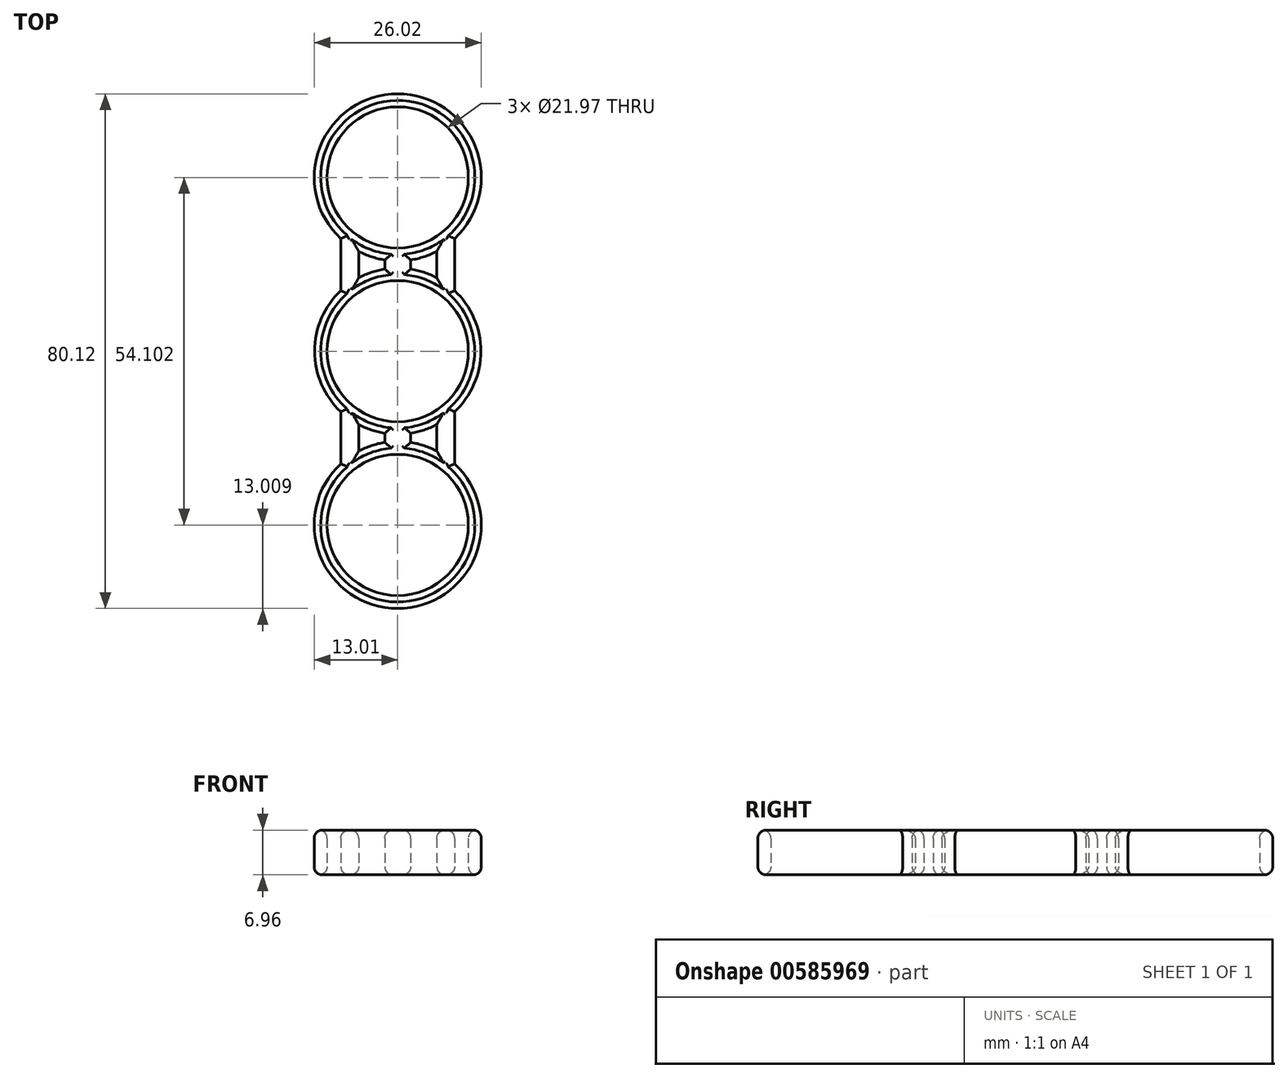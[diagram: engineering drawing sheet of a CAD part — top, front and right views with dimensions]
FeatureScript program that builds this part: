
annotation { "Feature Type Name" : "Feature", "Feature Type Description" : "" }
export const myFeature = defineFeature(function(context is Context, id is Id, definition is map)
    precondition{}
    {
        {
            var Q0;
            Q0=qCreatedBy(makeId("Top.planeOp"),FACE);
            var sketch = newSketch(context, id + "F0", { "sketchPlane" : qUnion([Q0])});
            skCircle(sketch, "E0", {"center": v(0, 0) * mm, "radius": 10.99 * mm});
            skCircle(sketch, "E1", {"center": v(0, 27.05) * mm, "radius": 10.99 * mm});
            skCircle(sketch, "E2", {"center": v(0, -27.05) * mm, "radius": 10.99 * mm});
            skArc(sketch, "E3", {"start": v(-8.86, 9.43) * mm, "mid": v(-12.94, 0) * mm, "end": v(-8.86, -9.43) * mm});
            skArc(sketch, "E4", {"start": v(-6.08, 15.55) * mm, "mid": v(-4.1, 14.7) * mm, "end": v(-2.02, 14.2) * mm});
            skArc(sketch, "E5.MirrorC", {"start": v(-6.08, -15.55) * mm, "mid": v(-4.1, -14.7) * mm, "end": v(-2.02, -14.2) * mm});
            skLineSegment(sketch, "E6", {"start": v(-8.86, -9.43) * mm, "end": v(-8.86, -17.53) * mm});
            skLineSegment(sketch, "E7", {"start": v(-6.08, -11.42) * mm, "end": v(-6.08, -15.55) * mm});
            skLineSegment(sketch, "E8", {"start": v(-2.02, -12.78) * mm, "end": v(-2.02, -14.2) * mm});
            skLineSegment(sketch, "E9.MirrorCS", {"start": v(2.02, -12.78) * mm, "end": v(2.02, -14.2) * mm});
            skLineSegment(sketch, "E10.MirrorCS", {"start": v(6.08, -11.42) * mm, "end": v(6.08, -15.55) * mm});
            skLineSegment(sketch, "E11.MirrorCS", {"start": v(8.86, -9.43) * mm, "end": v(8.86, -17.53) * mm});
            skLineSegment(sketch, "E12.MirrorCS", {"start": v(-8.86, 9.43) * mm, "end": v(-8.86, 17.53) * mm});
            skLineSegment(sketch, "E13.MirrorCS", {"start": v(-6.08, 11.42) * mm, "end": v(-6.08, 15.55) * mm});
            skLineSegment(sketch, "E14.MirrorCS", {"start": v(-2.02, 12.78) * mm, "end": v(-2.02, 14.2) * mm});
            skLineSegment(sketch, "E15.MirrorCS", {"start": v(2.02, 12.78) * mm, "end": v(2.02, 14.2) * mm});
            skLineSegment(sketch, "E16.MirrorCS", {"start": v(6.08, 11.42) * mm, "end": v(6.08, 15.55) * mm});
            skLineSegment(sketch, "E17.MirrorCS", {"start": v(8.86, 9.43) * mm, "end": v(8.86, 17.53) * mm});
            skPoint(sketch, "E18.orphan", {"position": v(-69.54, 0) * mm});
            skPoint(sketch, "E19.orphan", {"position": v(0, 58.4) * mm});
            skArc(sketch, "E20.trimOffspring", {"start": v(2.02, 14.2) * mm, "mid": v(4.1, 14.7) * mm, "end": v(6.08, 15.55) * mm});
            skArc(sketch, "E21.trimOffspring", {"start": v(-2.02, 12.78) * mm, "mid": v(-4.1, 12.27) * mm, "end": v(-6.08, 11.42) * mm});
            skArc(sketch, "E22.trimOffspring", {"start": v(8.86, 17.53) * mm, "mid": v(0, 40.06) * mm, "end": v(-8.86, 17.53) * mm});
            skArc(sketch, "E23.trimOffspring", {"start": v(6.08, 11.42) * mm, "mid": v(4.1, 12.27) * mm, "end": v(2.02, 12.78) * mm});
            skArc(sketch, "E24.trimOffspring", {"start": v(-6.08, -11.42) * mm, "mid": v(-4.1, -12.27) * mm, "end": v(-2.02, -12.78) * mm});
            skArc(sketch, "E25.trimOffspring", {"start": v(2.02, -14.2) * mm, "mid": v(4.1, -14.7) * mm, "end": v(6.08, -15.55) * mm});
            skArc(sketch, "E26.trimOffspring", {"start": v(2.02, -12.78) * mm, "mid": v(4.1, -12.27) * mm, "end": v(6.08, -11.42) * mm});
            skArc(sketch, "E27.trimOffspring", {"start": v(8.86, -9.43) * mm, "mid": v(12.94, 0) * mm, "end": v(8.86, 9.43) * mm});
            skArc(sketch, "E28.trimOffspring", {"start": v(8.86, -17.53) * mm, "mid": v(0, -40.06) * mm, "end": v(-8.86, -17.53) * mm});
            skSolve(sketch);
        }
        {
            var Q0;
            Q0 = qSketchRegion(id + "F0", true);
            extrude(context, id + "F1", {"entities" : qUnion([Q0]), "depth" : 6.96 * mm, "offsetDistance" : 25.4 * mm});
        }
        {
            var Q0;
            Q0=makeQuery(id+"F1.opExtrude","CAP_FACE",FACE,{"disambiguationData":[OSD([sQuery(id+"F0.wireOp",EDGE,"E0"),sQuery(id+"F0.wireOp",EDGE,"E1"),sQuery(id+"F0.wireOp",EDGE,"E2"),sQuery(id+"F0.wireOp",EDGE,"E3"),sQuery(id+"F0.wireOp",EDGE,"E4"),sQuery(id+"F0.wireOp",EDGE,"E5.MirrorC"),sQuery(id+"F0.wireOp",EDGE,"E6"),sQuery(id+"F0.wireOp",EDGE,"E7"),sQuery(id+"F0.wireOp",EDGE,"E8"),sQuery(id+"F0.wireOp",EDGE,"E9.MirrorCS"),sQuery(id+"F0.wireOp",EDGE,"E10.MirrorCS"),sQuery(id+"F0.wireOp",EDGE,"E11.MirrorCS"),sQuery(id+"F0.wireOp",EDGE,"E12.MirrorCS"),sQuery(id+"F0.wireOp",EDGE,"E13.MirrorCS"),sQuery(id+"F0.wireOp",EDGE,"E14.MirrorCS"),sQuery(id+"F0.wireOp",EDGE,"E15.MirrorCS"),sQuery(id+"F0.wireOp",EDGE,"E16.MirrorCS"),sQuery(id+"F0.wireOp",EDGE,"E17.MirrorCS"),sQuery(id+"F0.wireOp",EDGE,"E20.trimOffspring"),sQuery(id+"F0.wireOp",EDGE,"E21.trimOffspring"),sQuery(id+"F0.wireOp",EDGE,"E22.trimOffspring"),sQuery(id+"F0.wireOp",EDGE,"E23.trimOffspring"),sQuery(id+"F0.wireOp",EDGE,"E24.trimOffspring"),sQuery(id+"F0.wireOp",EDGE,"E25.trimOffspring"),sQuery(id+"F0.wireOp",EDGE,"E26.trimOffspring"),sQuery(id+"F0.wireOp",EDGE,"E27.trimOffspring"),sQuery(id+"F0.wireOp",EDGE,"E28.trimOffspring")])],"isStart":false});
            var Q1;
            Q1=makeQuery(id+"F1.opExtrude","CAP_FACE",FACE,{"disambiguationData":[OSD([sQuery(id+"F0.wireOp",EDGE,"E0"),sQuery(id+"F0.wireOp",EDGE,"E1"),sQuery(id+"F0.wireOp",EDGE,"E2"),sQuery(id+"F0.wireOp",EDGE,"E3"),sQuery(id+"F0.wireOp",EDGE,"E4"),sQuery(id+"F0.wireOp",EDGE,"E5.MirrorC"),sQuery(id+"F0.wireOp",EDGE,"E6"),sQuery(id+"F0.wireOp",EDGE,"E7"),sQuery(id+"F0.wireOp",EDGE,"E8"),sQuery(id+"F0.wireOp",EDGE,"E9.MirrorCS"),sQuery(id+"F0.wireOp",EDGE,"E10.MirrorCS"),sQuery(id+"F0.wireOp",EDGE,"E11.MirrorCS"),sQuery(id+"F0.wireOp",EDGE,"E12.MirrorCS"),sQuery(id+"F0.wireOp",EDGE,"E13.MirrorCS"),sQuery(id+"F0.wireOp",EDGE,"E14.MirrorCS"),sQuery(id+"F0.wireOp",EDGE,"E15.MirrorCS"),sQuery(id+"F0.wireOp",EDGE,"E16.MirrorCS"),sQuery(id+"F0.wireOp",EDGE,"E17.MirrorCS"),sQuery(id+"F0.wireOp",EDGE,"E20.trimOffspring"),sQuery(id+"F0.wireOp",EDGE,"E21.trimOffspring"),sQuery(id+"F0.wireOp",EDGE,"E22.trimOffspring"),sQuery(id+"F0.wireOp",EDGE,"E23.trimOffspring"),sQuery(id+"F0.wireOp",EDGE,"E24.trimOffspring"),sQuery(id+"F0.wireOp",EDGE,"E25.trimOffspring"),sQuery(id+"F0.wireOp",EDGE,"E26.trimOffspring"),sQuery(id+"F0.wireOp",EDGE,"E27.trimOffspring"),sQuery(id+"F0.wireOp",EDGE,"E28.trimOffspring")])],"isStart":true});
            fillet(context, id + "F2", {"entities" : qUnion([Q0, Q1]), "radius" : 1.27 * mm, "tangentPropagation" : true, "allowEdgeOverflow" : false});
        }
    });
